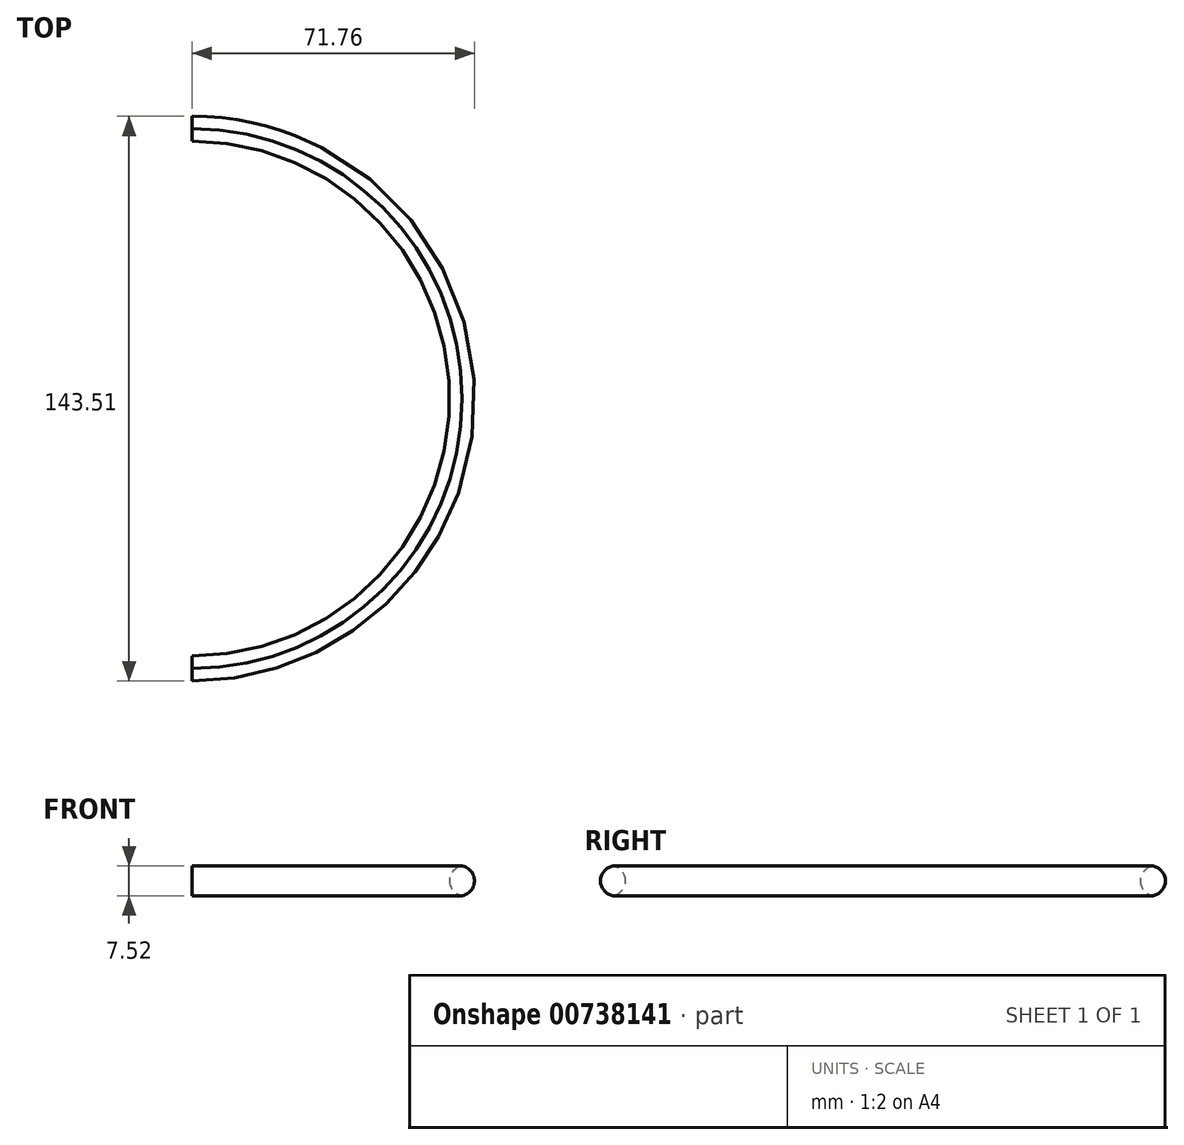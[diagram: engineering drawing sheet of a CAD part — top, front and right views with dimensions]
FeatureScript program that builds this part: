
annotation { "Feature Type Name" : "Feature", "Feature Type Description" : "" }
export const myFeature = defineFeature(function(context is Context, id is Id, definition is map)
    precondition{}
    {
        {
            var Q0;
            Q0=qCreatedBy(makeId("Top.planeOp"),FACE);
            var sketch = newSketch(context, id + "F0", { "sketchPlane" : qUnion([Q0])});
            skPoint(sketch, "E0.0", {"position": v(0, -68.1) * mm});
            skPoint(sketch, "E1.0", {"position": v(0, 75.41) * mm});
            skArc(sketch, "E2", {"start": v(0, -68.1) * mm, "mid": v(71.76, 3.66) * mm, "end": v(0, 75.41) * mm});
            skLineSegment(sketch, "E3", {"start": v(0, 75.41) * mm, "end": v(0, 69.06) * mm});
            skLineSegment(sketch, "E4", {"start": v(0, -68.1) * mm, "end": v(0, -61.75) * mm});
            skArc(sketch, "E5", {"start": v(0, -61.75) * mm, "mid": v(65.4, 3.66) * mm, "end": v(0, 69.06) * mm});
            skSolve(sketch);
        }
        {
            var Q0;
            Q0 = qSketchRegion(id + "F0", true);
            extrude(context, id + "F1", {"entities" : qUnion([Q0]), "depth" : 7.62 * mm, "offsetDistance" : 25.4 * mm});
        }
        {
            var Q0;
            Q0=makeQuery(id+"F1.opExtrude","CAP_EDGE",EDGE,{"disambiguationData":[OSD([sQuery(id+"F0.wireOp",EDGE,"E2")])],"isStart":false});
            var Q1;
            Q1=makeQuery(id+"F1.opExtrude","CAP_EDGE",EDGE,{"disambiguationData":[OSD([sQuery(id+"F0.wireOp",EDGE,"E5")])],"isStart":false});
            var Q2;
            Q2=makeQuery(id+"F1.opExtrude","CAP_EDGE",EDGE,{"disambiguationData":[OSD([sQuery(id+"F0.wireOp",EDGE,"E2")])],"isStart":true});
            var Q3;
            Q3=makeQuery(id+"F1.opExtrude","CAP_EDGE",EDGE,{"disambiguationData":[OSD([sQuery(id+"F0.wireOp",EDGE,"E5")])],"isStart":true});
            fillet(context, id + "F2", {"entities" : qUnion([Q0, Q1, Q2, Q3]), "radius" : 3.8 * mm, "tangentPropagation" : true, "allowEdgeOverflow" : false});
        }
    });
